# Revit family: sh-2404
name_source: partatom
category: Lighting Fixtures
revit_build: Autodesk Revit 2017 (Build: 20160225_1515(x64)
units: mm (PartAtom-declared; Revit-internal decimal feet)

## family parameters
Always vertical = Yes
Cut with Voids When Loaded = No
Host = Wall
Light Source = Yes
OmniClass Number = 23.80.70.00
OmniClass Title = Lighting
Part Type = Normal
Room Calculation Point = No
Round Connector Dimension = Use Diameter
Shared = Yes

## types (1)
- SH-2404(Black body-3000K-E27)
    Body Material = Aluminum
    Body color = Black Body
    Color Filter = 16777215
    Color Temperature = 3000K
    Cost = 0 $
    Diffuser Material = polycarbonate-anti uv
    Dimming Lamp Color Temperature Shift = <None>
    Emit Shape Visible in Rendering = No
    Emit from Circle Diameter = 40.0 cm
    Height = 25.0 cm
    IP = 54
    Instalation = Wall Mounted
    Lamp = E27
    Light Source Symbol Size = 40.0 cm
    Manufacturer = SHOA
    Model = SH-2404
    URL = https://www.shoaco.com
    Voltage/Frequency = 230 V Ac/50HZ
    Website = www.shoaco.com
    Width = 17.0 cm
    consumption current = 1 A
    protection class = class I
    wattage. = 9 W

## geometry (parser evidence)
native form markers: Sweep x2
no freeform markers — native parametric forms only
